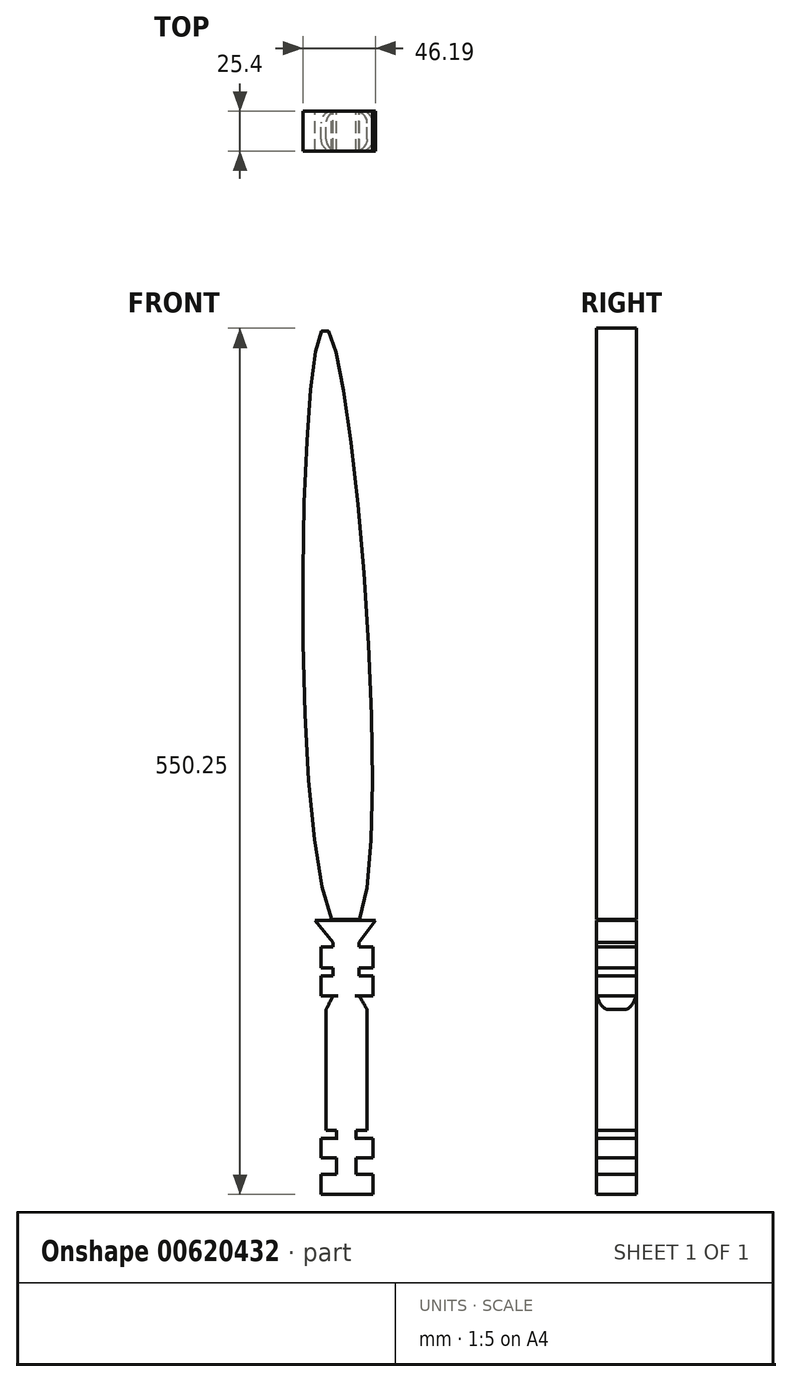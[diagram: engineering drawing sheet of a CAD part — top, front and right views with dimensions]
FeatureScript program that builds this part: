
annotation { "Feature Type Name" : "Feature", "Feature Type Description" : "" }
export const myFeature = defineFeature(function(context is Context, id is Id, definition is map)
    precondition{}
    {
        {
            var Q0;
            Q0=qCreatedBy(makeId("Front.planeOp"),FACE);
            var sketch = newSketch(context, id + "F0", { "sketchPlane" : qUnion([Q0])});
            skLineSegment(sketch, "E0.bottom", {"start": v(-26.01, -58.98) * mm, "end": v(0, -58.98) * mm});
            skLineSegment(sketch, "E0.top", {"start": v(-26.01, 17.95) * mm, "end": v(0, 17.95) * mm});
            skLineSegment(sketch, "E0.left", {"start": v(-26.01, -58.98) * mm, "end": v(-26.01, 17.95) * mm});
            skLineSegment(sketch, "E0.right", {"start": v(0, -58.98) * mm, "end": v(0, 17.95) * mm});
            skLineSegment(sketch, "E1", {"start": v(0, 17.95) * mm, "end": v(-5.04, 26.59) * mm});
            skLineSegment(sketch, "E2", {"start": v(-26.01, 17.95) * mm, "end": v(-21.7, 26.59) * mm});
            skLineSegment(sketch, "E3.bottom", {"start": v(-19.42, -58.98) * mm, "end": v(-6.96, -58.98) * mm});
            skLineSegment(sketch, "E3.top", {"start": v(-19.42, -93.37) * mm, "end": v(-6.96, -93.37) * mm});
            skLineSegment(sketch, "E3.left", {"start": v(-19.42, -58.98) * mm, "end": v(-19.42, -93.37) * mm});
            skLineSegment(sketch, "E3.right", {"start": v(-6.96, -58.98) * mm, "end": v(-6.96, -93.37) * mm});
            skLineSegment(sketch, "E4.bottom", {"start": v(-5.04, 26.59) * mm, "end": v(-19.42, 26.59) * mm});
            skLineSegment(sketch, "E5.bottom", {"start": v(-29.38, 57.76) * mm, "end": v(3.72, 57.76) * mm});
            skLineSegment(sketch, "E5.top", {"start": v(-29.38, 44.52) * mm, "end": v(3.72, 44.52) * mm});
            skLineSegment(sketch, "E5.left", {"start": v(-29.38, 57.76) * mm, "end": v(-29.38, 44.52) * mm});
            skLineSegment(sketch, "E5.right", {"start": v(3.72, 57.76) * mm, "end": v(3.72, 44.52) * mm});
            skPoint(sketch, "E6.oppositeSnap0", {"position": v(-6.96, -76.18) * mm});
            skLineSegment(sketch, "E6.bottom", {"start": v(-29.38, -63.93) * mm, "end": v(3.72, -63.93) * mm});
            skLineSegment(sketch, "E6.top", {"start": v(-29.38, -76.18) * mm, "end": v(3.72, -76.18) * mm});
            skLineSegment(sketch, "E6.left", {"start": v(-29.38, -63.93) * mm, "end": v(-29.38, -76.18) * mm});
            skLineSegment(sketch, "E6.right", {"start": v(3.72, -63.93) * mm, "end": v(3.72, -76.18) * mm});
            skLineSegment(sketch, "E7.bottom", {"start": v(-29.38, -99.56) * mm, "end": v(3.72, -99.56) * mm});
            skLineSegment(sketch, "E7.top", {"start": v(-29.38, -86.84) * mm, "end": v(3.72, -86.84) * mm});
            skLineSegment(sketch, "E7.left", {"start": v(-29.38, -99.56) * mm, "end": v(-29.38, -86.84) * mm});
            skLineSegment(sketch, "E7.right", {"start": v(3.72, -99.56) * mm, "end": v(3.72, -86.84) * mm});
            skLineSegment(sketch, "E8.bottom", {"start": v(-21.7, 26.59) * mm, "end": v(-5.04, 26.59) * mm});
            skLineSegment(sketch, "E8.top", {"start": v(-21.7, 60.7) * mm, "end": v(-5.04, 60.7) * mm});
            skLineSegment(sketch, "E8.left", {"start": v(-21.7, 26.59) * mm, "end": v(-21.7, 60.7) * mm});
            skLineSegment(sketch, "E8.right", {"start": v(-5.04, 26.59) * mm, "end": v(-5.04, 60.7) * mm});
            skLineSegment(sketch, "E9.bottom", {"start": v(3.72, 26.59) * mm, "end": v(-29.38, 26.59) * mm});
            skLineSegment(sketch, "E9.top", {"start": v(3.72, 39.21) * mm, "end": v(-29.38, 39.21) * mm});
            skLineSegment(sketch, "E9.left", {"start": v(3.72, 26.59) * mm, "end": v(3.72, 39.21) * mm});
            skLineSegment(sketch, "E9.right", {"start": v(-29.38, 26.59) * mm, "end": v(-29.38, 39.21) * mm});
            skLineSegment(sketch, "E10", {"start": v(-21.7, 60.7) * mm, "end": v(-32.93, 74.43) * mm});
            skLineSegment(sketch, "E11", {"start": v(-32.93, 74.43) * mm, "end": v(5.46, 74.43) * mm});
            skLineSegment(sketch, "E12", {"start": v(5.46, 74.43) * mm, "end": v(-5.04, 60.7) * mm});
            skSolve(sketch);
        }
        {
            var Q0;
            Q0 = qSketchRegion(id + "F0", true);
            extrude(context, id + "F1", {"entities" : qUnion([Q0]), "depth" : 25.4 * mm, "offsetDistance" : 25.4 * mm});
        }
        {
            var Q0;
            Q0=makeQuery(id+"F1.opExtrude","CAP_EDGE",EDGE,{"disambiguationData":[OSD([sQuery(id+"F0.wireOp",EDGE,"E0.right")])],"isStart":false});
            var Q1;
            Q1=makeQuery(id+"F1.opExtrude","CAP_EDGE",EDGE,{"disambiguationData":[OSD([sQuery(id+"F0.wireOp",EDGE,"E0.left")])],"isStart":false});
            var Q2;
            Q2=makeQuery(id+"F1.opExtrude","CAP_EDGE",EDGE,{"disambiguationData":[OSD([sQuery(id+"F0.wireOp",EDGE,"E0.left")])],"isStart":true});
            var Q3;
            Q3=makeQuery(id+"F1.opExtrude","CAP_EDGE",EDGE,{"disambiguationData":[OSD([sQuery(id+"F0.wireOp",EDGE,"E0.right")])],"isStart":true});
            var Q4;
            Q4=makeQuery(id+"F1.opExtrude","CAP_EDGE",EDGE,{"disambiguationData":[OSD([sQuery(id+"F0.wireOp",EDGE,"E9.left")])],"isStart":false});
            var Q5;
            Q5=makeQuery(id+"F1.opExtrude","CAP_EDGE",EDGE,{"disambiguationData":[OSD([sQuery(id+"F0.wireOp",EDGE,"E9.left")])],"isStart":true});
            var Q6;
            Q6=makeQuery(id+"F1.opExtrude","CAP_EDGE",EDGE,{"disambiguationData":[OSD([sQuery(id+"F0.wireOp",EDGE,"E9.right")])],"isStart":false});
            var Q7;
            Q7=makeQuery(id+"F1.opExtrude","CAP_EDGE",EDGE,{"disambiguationData":[OSD([sQuery(id+"F0.wireOp",EDGE,"E9.right")])],"isStart":true});
            var Q8;
            Q8=makeQuery(id+"F1.opExtrude","CAP_EDGE",EDGE,{"disambiguationData":[OSD([sQuery(id+"F0.wireOp",EDGE,"E5.right")])],"isStart":false});
            var Q9;
            Q9=makeQuery(id+"F1.opExtrude","CAP_EDGE",EDGE,{"disambiguationData":[OSD([sQuery(id+"F0.wireOp",EDGE,"E5.left")])],"isStart":false});
            var Q10;
            Q10=makeQuery(id+"F1.opExtrude","CAP_EDGE",EDGE,{"disambiguationData":[OSD([sQuery(id+"F0.wireOp",EDGE,"E6.right")])],"isStart":false});
            var Q11;
            Q11=makeQuery(id+"F1.opExtrude","CAP_EDGE",EDGE,{"disambiguationData":[OSD([sQuery(id+"F0.wireOp",EDGE,"E6.left")])],"isStart":false});
            var Q12;
            Q12=makeQuery(id+"F1.opExtrude","CAP_EDGE",EDGE,{"disambiguationData":[OSD([sQuery(id+"F0.wireOp",EDGE,"E7.left")])],"isStart":false});
            var Q13;
            Q13=makeQuery(id+"F1.opExtrude","CAP_EDGE",EDGE,{"disambiguationData":[OSD([sQuery(id+"F0.wireOp",EDGE,"E7.right")])],"isStart":false});
            var Q14;
            Q14=makeQuery(id+"F1.opExtrude","CAP_EDGE",EDGE,{"disambiguationData":[OSD([sQuery(id+"F0.wireOp",EDGE,"E7.right")])],"isStart":true});
            var Q15;
            Q15=makeQuery(id+"F1.opExtrude","CAP_EDGE",EDGE,{"disambiguationData":[OSD([sQuery(id+"F0.wireOp",EDGE,"E6.right")])],"isStart":true});
            var Q16;
            Q16=makeQuery(id+"F1.opExtrude","CAP_EDGE",EDGE,{"disambiguationData":[OSD([sQuery(id+"F0.wireOp",EDGE,"E6.left")])],"isStart":true});
            var Q17;
            Q17=makeQuery(id+"F1.opExtrude","CAP_EDGE",EDGE,{"disambiguationData":[OSD([sQuery(id+"F0.wireOp",EDGE,"E7.left")])],"isStart":true});
            var Q18;
            Q18=makeQuery(id+"F1.opExtrude","CAP_EDGE",EDGE,{"disambiguationData":[OSD([sQuery(id+"F0.wireOp",EDGE,"E5.left")])],"isStart":true});
            var Q19;
            Q19=makeQuery(id+"F1.opExtrude","CAP_EDGE",EDGE,{"disambiguationData":[OSD([sQuery(id+"F0.wireOp",EDGE,"E5.right")])],"isStart":true});
            fillet(context, id + "F2", {"entities" : qUnion([Q0, Q1, Q2, Q3, Q4, Q5, Q6, Q7, Q8, Q9, Q10, Q11, Q12, Q13, Q14, Q15, Q16, Q17, Q18, Q19]), "radius" : 7.62 * mm, "tangentPropagation" : true, "allowEdgeOverflow" : false});
        }
        {
            var Q0;
            Q0=qCreatedBy(makeId("Front.planeOp"),FACE);
            var sketch = newSketch(context, id + "F3", { "sketchPlane" : qUnion([Q0])});
            skFitSpline(sketch, "E13", {"points": [v(-22.6, 75.37) * mm, v(-4.83, 75) * mm, v(-26.76, 450.7) * mm, v(-22.6, 75.37) * mm]});
            skFitSpline(sketch, "E14", {"points": [v(-4.83, 75) * mm, v(-22.6, 75.37) * mm], "startDerivative": vector(-17.76, 0.37) * mm, "endDerivative": vector(-17.76, 0.37) * mm});
            skSolve(sketch);
        }
        {
            var Q0;
            {var subQ0=sQuery(id+"F3.wireOp",EDGE,"E14");Q0=makeQuery(id+"F3.imprint","IMPRINT",FACE,{"disambiguationData":[TD([[makeQuery(id+"F3.imprint","IMPRINT",EDGE,{"derivedFrom":subQ0}),-1.0]])]});}
            extrude(context, id + "F4", {"entities" : qUnion([Q0]), "depth" : 25.4 * mm, "offsetDistance" : 25.4 * mm});
        }
    });
